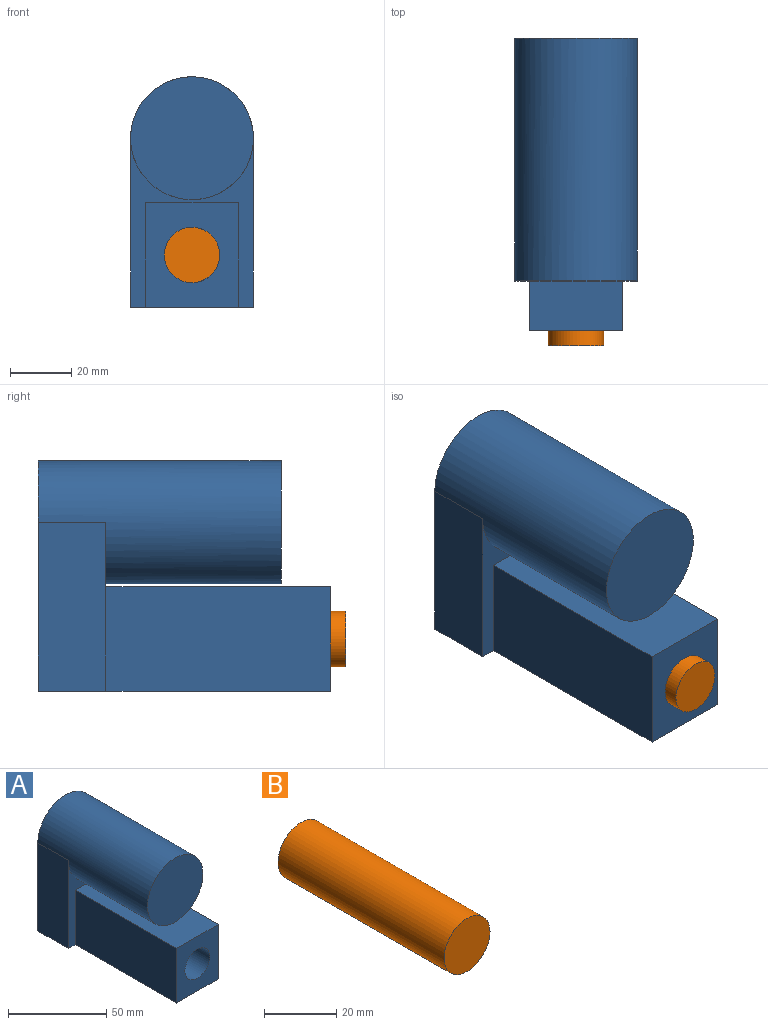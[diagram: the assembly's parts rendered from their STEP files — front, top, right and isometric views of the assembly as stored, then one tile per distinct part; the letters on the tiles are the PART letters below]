
ASSEMBLY  parts=2 mates=1
PART A: 13 faces, bbox 40x95x75 mm
  f0: cylinder r=20mm len=79mm, axis (0,1,0), area 8545.1mm2, adj f1,f2,f8,f9,f10
  f1: plane 40x40mm, normal (0,-1,0), area 1256.6mm2, adj f0
  f2: plane 75x40mm, normal (0,1,0), area 2828.3mm2, adj f0,f5,f8,f9
  f3: plane 73x30mm, normal (0,0,1), area 2190mm2, adj f4,f6,f7,f10
  f4: plane 73x34mm, normal (-1,0,0), area 2482mm2, adj f3,f5,f7,f10
  f5: plane 95x40mm, normal (0,0,-1), area 3070mm2, adj f2,f4,f6,f7,f8,f9,f10
  f6: plane 73x34mm, normal (1,0,0), area 2482mm2, adj f3,f5,f7,f10
  f7: plane 34x30mm, normal (0,-1,0), area 765.5mm2, adj f3,f4,f5,f6,f11
  f8: plane 55x22mm, normal (-1,0,0), area 1210mm2, adj f0,f2,f5,f10
  f9: plane 55x22mm, normal (1,0,0), area 1210mm2, adj f0,f2,f5,f10
  f10: plane 55x40mm, normal (0,-1,0), area 551.7mm2, adj f0,f3,f4,f5,f6,f8,f9
  f11: cylinder r=9mm len=70mm, axis (0,-1,0), area 3958.4mm2, adj f7,f12
  f12: plane 18x18mm, normal (0,-1,0), area 254.5mm2, adj f11
PART B: 3 faces, bbox 18x65x18 mm
  f0: cylinder r=9mm len=65mm, axis (0,1,0), area 3675.7mm2, adj f1,f2
  f1: plane 18x18mm, normal (0,-1,0), area 254.5mm2, adj f0
  f2: plane 18x18mm, normal (0,1,0), area 254.5mm2, adj f0
PLACE A rot(axis=(0,-1,0),0deg) t=(-90.68,12.4,6.78)mm fixed
PLACE B rot(axis=(0,-1,0),109.5deg) t=(-126.49,39.9,-43.94)mm
MATE cylindrical A.f11 <-> B.f0  axis (0,-1,0) through (-90.68,-82.6,-31.22)mm
